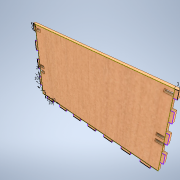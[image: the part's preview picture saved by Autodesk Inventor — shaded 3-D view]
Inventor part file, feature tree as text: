
AUTODESK INVENTOR PART (.ipt)
format: ipt  version: 2021 (Build 250183000, 183)  size: 239,616 bytes
history: native  units: mm
features: extrude x3, sketch x3
ambient origin geometry x8: Origin, YZ Plane, XZ Plane, XY Plane, X Axis, Y Axis, Z Axis, Center Point
bodies: Solid1 (feature_tree)
feature tree (6):
  extrude  "Extrusion1"  Depth=77.0mm
  extrude  "Extrusion2"  Depth=3.0mm
  extrude  "Extrusion3"  Depth=70.0mm
  sketch  "Sketch1"  dims[d0=144.0mm d1=77.0mm]
  sketch  "Sketch2"  dims[d2=3.0mm d3=0.0mm d4=3.0mm]
  sketch  "Sketch3"  dims[d5=10.0mm d6=70.0mm d8=20.0mm d9=10.0mm d11=10.0mm d13=3.0mm d14=10.0mm d15=30.0mm d17=20.0mm d18=10.0mm d20=10.0mm d22=3.0mm d23=7.0mm d24=3.0mm d25=3.0mm d26=0.0mm d27=7.0mm d28=3.0mm d29=20.0mm d31=137.0mm d32=20.0mm d34=38.0mm d37=0.0mm d38=0.0mm d39=20.0mm d41=6.5mm d42=20.0mm d44=137.0mm d47=3.5mm d48=3.5mm]
